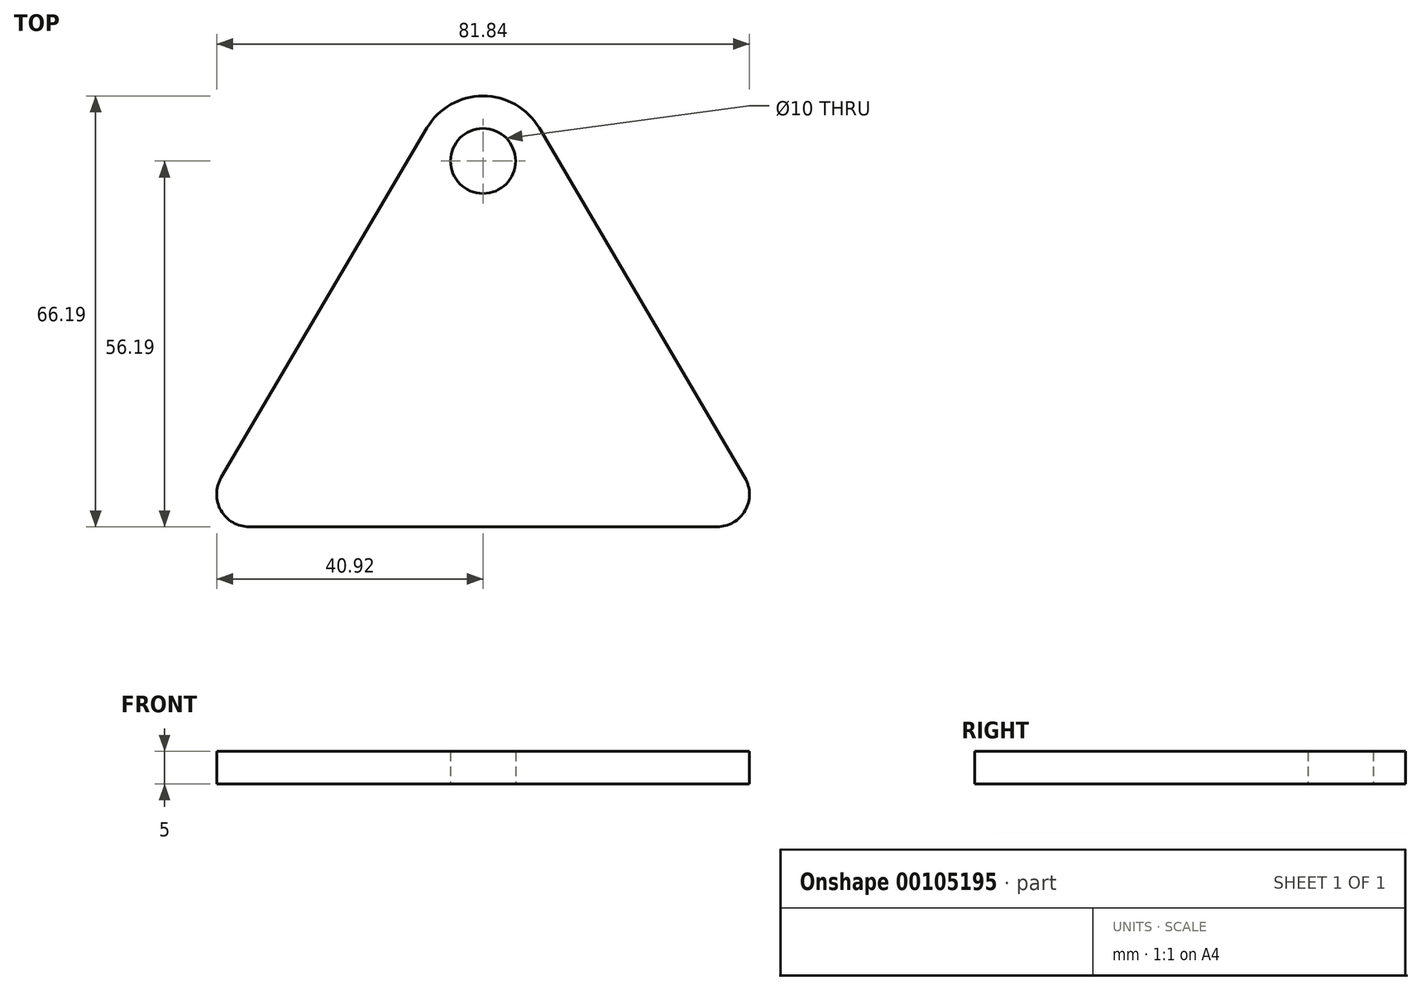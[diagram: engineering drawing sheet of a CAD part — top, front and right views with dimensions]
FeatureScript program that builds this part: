
annotation { "Feature Type Name" : "Feature", "Feature Type Description" : "" }
export const myFeature = defineFeature(function(context is Context, id is Id, definition is map)
    precondition{}
    {
        {
            var Q0;
            Q0=qCreatedBy(makeId("Top.planeOp"),FACE);
            var sketch = newSketch(context, id + "F0", { "sketchPlane" : qUnion([Q0])});
            skCircle(sketch, "E0", {"center": v(0, 0) * mm, "radius": 5 * mm});
            skLineSegment(sketch, "E1", {"start": v(0, -56.2) * mm, "end": v(-35.92, -56.2) * mm});
            skArc(sketch, "E2.0", {"start": v(8.62, 5.07) * mm, "mid": v(0, 10) * mm, "end": v(-8.62, 5.07) * mm});
            skLineSegment(sketch, "E3", {"start": v(-40.23, -48.66) * mm, "end": v(-8.62, 5.07) * mm});
            skLineSegment(sketch, "E4.MirrorCS", {"start": v(40.23, -48.66) * mm, "end": v(8.62, 5.07) * mm});
            skLineSegment(sketch, "E5.MirrorCS", {"start": v(0, -56.2) * mm, "end": v(35.92, -56.2) * mm});
            skPoint(sketch, "E6.visualSharp", {"position": v(-44.66, -56.2) * mm});
            skArc(sketch, "E6.filletArc", {"start": v(-40.23, -48.66) * mm, "mid": v(-40.26, -53.67) * mm, "end": v(-35.92, -56.2) * mm});
            skPoint(sketch, "E7.visualSharp", {"position": v(44.66, -56.2) * mm});
            skArc(sketch, "E7.filletArc", {"start": v(35.92, -56.2) * mm, "mid": v(40.26, -53.67) * mm, "end": v(40.23, -48.66) * mm});
            skSolve(sketch);
        }
        {
            var Q0;
            Q0=makeQuery(id+"F0.imprint","IMPRINT",FACE,{"disambiguationData":[TD([[makeQuery(id+"F0.imprint","IMPRINT",EDGE,{"derivedFrom":sQuery(id+"F0.wireOp",EDGE,"E0")}),-1.0]])]});
            extrude(context, id + "F1", {"entities" : qUnion([Q0]), "depth" : 5 * mm});
        }
    });
